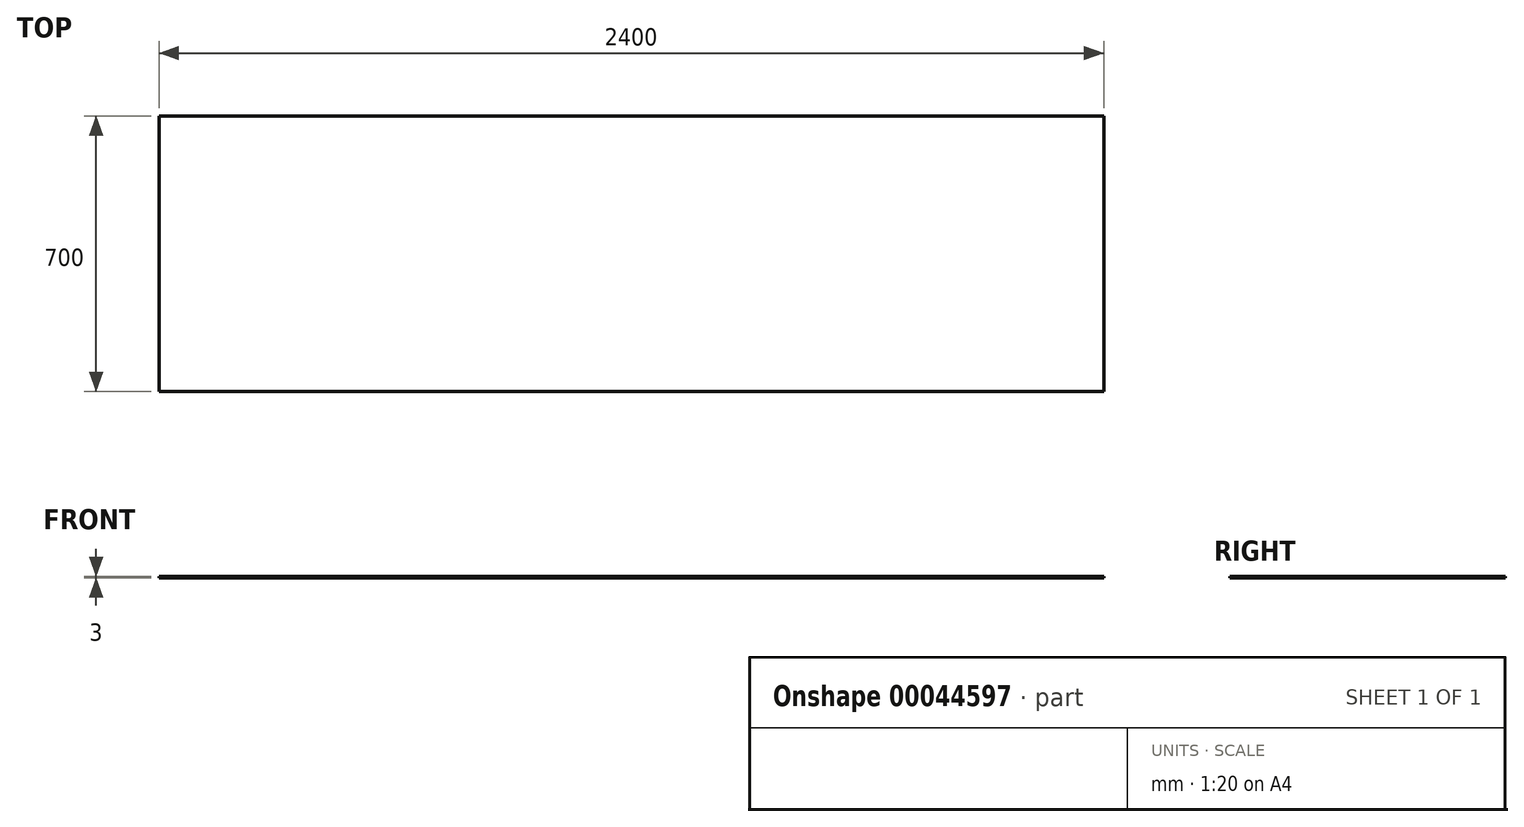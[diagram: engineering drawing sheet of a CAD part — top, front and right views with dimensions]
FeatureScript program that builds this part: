
annotation { "Feature Type Name" : "Feature", "Feature Type Description" : "" }
export const myFeature = defineFeature(function(context is Context, id is Id, definition is map)
    precondition{}
    {
        {
            var Q0;
            Q0=qCreatedBy(makeId("Top.planeOp"),FACE);
            var sketch = newSketch(context, id + "F0", { "sketchPlane" : qUnion([Q0])});
            skLineSegment(sketch, "E0.rect.bottom", {"start": v(1200, 350) * mm, "end": v(-1200, 350) * mm});
            skLineSegment(sketch, "E0.rect.top", {"start": v(1200, -350) * mm, "end": v(-1200, -350) * mm});
            skLineSegment(sketch, "E0.rect.left", {"start": v(1200, 350) * mm, "end": v(1200, -350) * mm});
            skLineSegment(sketch, "E0.rect.right", {"start": v(-1200, 350) * mm, "end": v(-1200, -350) * mm});
            skPoint(sketch, "E0.rect.middle", {"position": v(0, 0) * mm});
            skSolve(sketch);
        }
        {
            var Q0;
            Q0 = qSketchRegion(id + "F0", true);
            extrude(context, id + "F1", {"entities" : qUnion([Q0]), "depth" : 3 * mm});
        }
    });
